# Revit family: Boiler-Weil_McLain-Simplicity-199MBH
name_source: partatom
category: Mechanical Equipment
units: mm (PartAtom-declared; Revit-internal decimal feet)

## family parameters
Cut with Voids When Loaded = No
Host = Face
OmniClass Number = 23.75.10.11.14.14
OmniClass Title = Condensing Boilers
Part Type = Normal
Room Calculation Point = No
Round Connector Dimension = Use Diameter
Shared = No

## types (1)
- 199-C
    Boiler In Connection = 0' - 1"
    Boiler In Description = Male NPT
    Boiler Out Connection = 0' - 1"
    Boiler Out Description = Male NPT
    Condensate Tube Connection = 0' - 0 13/16"
    Default Elevation = 0' - 0"
    Depth = 1' - 8"
    Description = Gas Boiler
    Frequency = 60 Hz
    Gas Supply Connection Description = Male NPT
    Gas Supply Connection Diameter = 1"
    Height = 2' - 10"
    Hot Water Connection Description = Male NPT
    Hot Water Connection Diameter = 1"
    Manufacturer = Weil-McLain®
    Maximum Input Rate = 150000.0 Btu/h
    Model = 199-C
    Number of Poles = 1
    Phase = 1
    Power Factor = 1
    Product Name = Simplicity™
    Tank Capacity = 3.8 gal.
    URL = https://www.weil-mclain.com
    Weight = 122 lb.
    Width = 1' - 8"

## geometry (parser evidence)
native form markers: Blend x12, Sweep x2
no freeform markers — native parametric forms only
